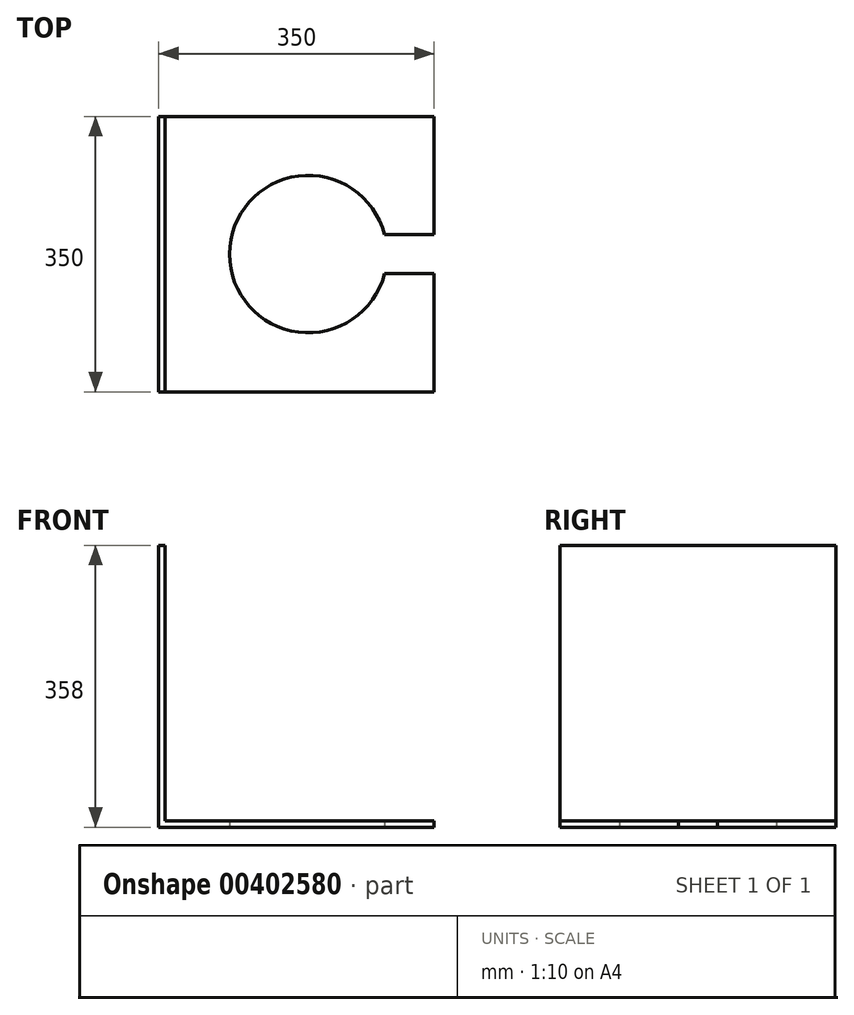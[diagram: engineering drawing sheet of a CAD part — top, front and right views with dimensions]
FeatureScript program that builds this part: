
annotation { "Feature Type Name" : "Feature", "Feature Type Description" : "" }
export const myFeature = defineFeature(function(context is Context, id is Id, definition is map)
    precondition{}
    {
        {
            var Q0;
            Q0=qCreatedBy(makeId("Top.planeOp"),FACE);
            var sketch = newSketch(context, id + "F0", { "sketchPlane" : qUnion([Q0])});
            skLineSegment(sketch, "E0", {"start": v(0, 0) * mm, "end": v(0, -350) * mm});
            skLineSegment(sketch, "E1", {"start": v(0, -350) * mm, "end": v(350, -350) * mm});
            skLineSegment(sketch, "E2", {"start": v(0, 0) * mm, "end": v(350, 0) * mm});
            skLineSegment(sketch, "E3", {"start": v(350, 0) * mm, "end": v(350, -350) * mm});
            skLineSegment(sketch, "E4", {"start": v(350, -350) * mm, "end": v(350, -200) * mm});
            skLineSegment(sketch, "E5", {"start": v(350, -200) * mm, "end": v(350, -150) * mm});
            skLineSegment(sketch, "E6", {"start": v(350, -200) * mm, "end": v(300, -200) * mm});
            skLineSegment(sketch, "E7", {"start": v(350, -150) * mm, "end": v(300, -150) * mm});
            skArc(sketch, "E8", {"start": v(286.82, -150) * mm, "mid": v(90, -175) * mm, "end": v(286.82, -200) * mm});
            skPoint(sketch, "E9.start.orphan", {"position": v(300, -175) * mm});
            skLineSegment(sketch, "E10", {"start": v(300, -200) * mm, "end": v(286.82, -200) * mm});
            skLineSegment(sketch, "E11", {"start": v(300, -150) * mm, "end": v(286.82, -150) * mm});
            skSolve(sketch);
        }
        {
            var Q0;
            Q0=makeQuery(id+"F0.imprint","IMPRINT",FACE,{"disambiguationData":[TD([[makeQuery(id+"F0.imprint","IMPRINT",EDGE,{"derivedFrom":sQuery(id+"F0.wireOp",EDGE,"E0")}),1.0]])]});
            extrude(context, id + "F1", {"entities" : qUnion([Q0]), "depth" : 8 * mm});
        }
        {
            var Q0;
            Q0=qCreatedBy(makeId("Right.planeOp"),FACE);
            var sketch = newSketch(context, id + "F2", { "sketchPlane" : qUnion([Q0])});
            skLineSegment(sketch, "E12", {"start": v(0, 0) * mm, "end": v(0, 358) * mm});
            skLineSegment(sketch, "E13", {"start": v(0, 358) * mm, "end": v(-350, 358) * mm});
            skLineSegment(sketch, "E14", {"start": v(-350, 358) * mm, "end": v(-350, 0) * mm});
            skLineSegment(sketch, "E15", {"start": v(-350, 0) * mm, "end": v(0, 0) * mm});
            skSolve(sketch);
        }
        {
            var Q0;
            Q0=makeQuery(id+"F2.imprint","IMPRINT",FACE,{"disambiguationData":[TD([[makeQuery(id+"F2.imprint","IMPRINT",EDGE,{"derivedFrom":sQuery(id+"F2.wireOp",EDGE,"E12")}),1.0]])]});
            extrude(context, id + "F3", {"entities" : qUnion([Q0]), "operationType" : NewBodyOperationType.ADD, "depth" : 8 * mm});
        }
    });
